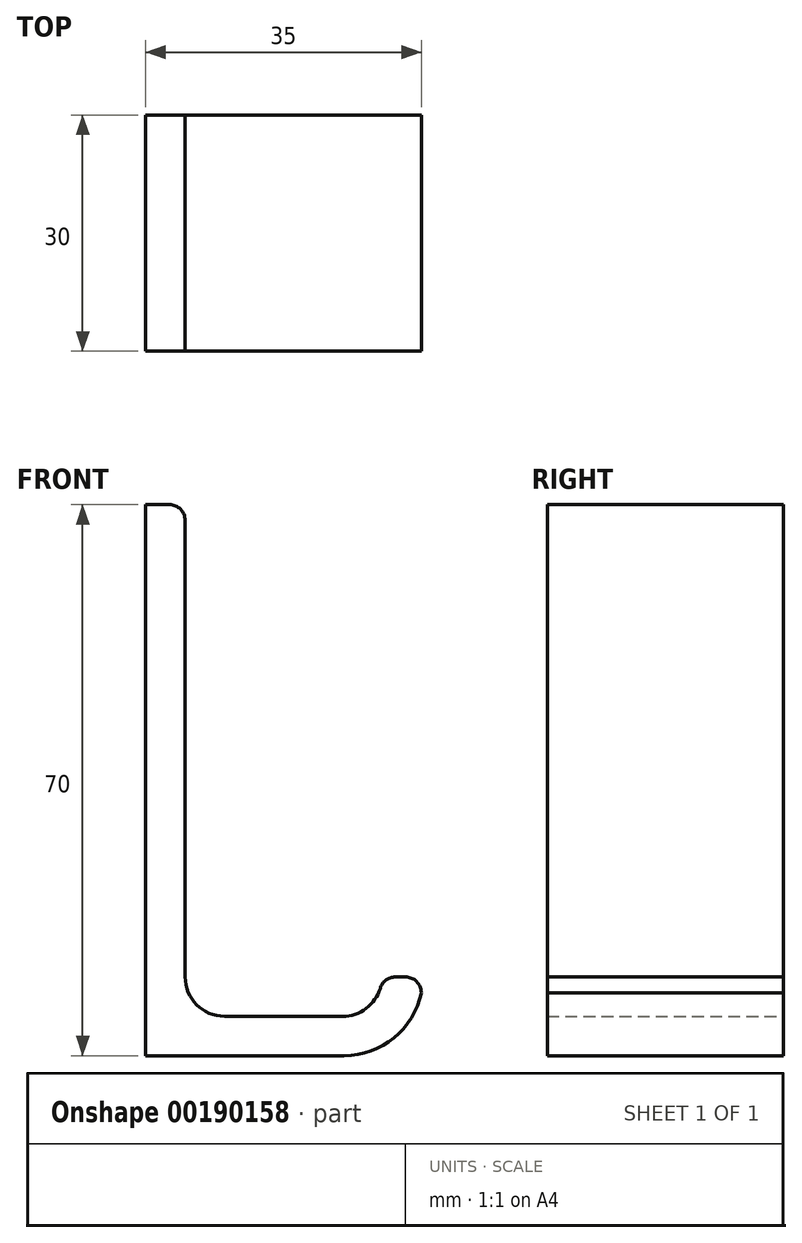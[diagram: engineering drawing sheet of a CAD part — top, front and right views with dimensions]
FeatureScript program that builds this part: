
annotation { "Feature Type Name" : "Feature", "Feature Type Description" : "" }
export const myFeature = defineFeature(function(context is Context, id is Id, definition is map)
    precondition{}
    {
        {
            var Q0;
            Q0=qCreatedBy(makeId("Front.planeOp"),FACE);
            var sketch = newSketch(context, id + "F0", { "sketchPlane" : qUnion([Q0])});
            skLineSegment(sketch, "E0.top", {"start": v(0, 70) * mm, "end": v(5, 70) * mm});
            skLineSegment(sketch, "E0.left", {"start": v(0, 0) * mm, "end": v(0, 70) * mm});
            skLineSegment(sketch, "E0.right", {"start": v(5, 5) * mm, "end": v(5, 70) * mm});
            skLineSegment(sketch, "E1.top", {"start": v(5, 5) * mm, "end": v(30, 5) * mm});
            skLineSegment(sketch, "E2.top", {"start": v(35, 10) * mm, "end": v(30, 10) * mm});
            skLineSegment(sketch, "E2.right", {"start": v(30, 5) * mm, "end": v(30, 10) * mm});
            skLineSegment(sketch, "E3", {"start": v(35, 10) * mm, "end": v(35, 0) * mm});
            skLineSegment(sketch, "E4", {"start": v(35, 0) * mm, "end": v(0, 0) * mm});
            skSolve(sketch);
        }
        {
            var Q0;
            Q0=qSketchRegion(id+"F0",true);
            extrude(context, id + "F1", {"entities" : qUnion([Q0]), "depth" : 30 * mm});
        }
        {
            var Q0;
            Q0=makeQuery(id+"F1.opExtrude","SWEPT_EDGE",EDGE,{"disambiguationData":[OSD([sQuery(id+"F0.wireOp",EDGE,"E0.right"),sQuery(id+"F0.wireOp",EDGE,"E1.top")])]});
            var Q1;
            Q1=makeQuery(id+"F1.opExtrude","SWEPT_EDGE",EDGE,{"disambiguationData":[OSD([sQuery(id+"F0.wireOp",EDGE,"E1.top"),sQuery(id+"F0.wireOp",EDGE,"E2.right")])]});
            fillet(context, id + "F2", {"entities" : qUnion([Q0, Q1]), "radius" : 5 * mm, "tangentPropagation" : true, "allowEdgeOverflow" : false});
        }
        {
            var Q0;
            Q0=makeQuery(id+"F2.opFillet","BLEND_EDGE",EDGE,{"blendedFrom":[makeQuery(id+"F1.opExtrude","SWEPT_EDGE",EDGE,{"disambiguationData":[OSD([sQuery(id+"F0.wireOp",EDGE,"E1.top"),sQuery(id+"F0.wireOp",EDGE,"E2.right")])]}),makeQuery(id+"F1.opExtrude","SWEPT_FACE",FACE,{"disambiguationData":[OSD([sQuery(id+"F0.wireOp",EDGE,"E2.top")])]})],"blendedInto":[makeQuery(id+"F1.opExtrude","SWEPT_FACE",FACE,{"disambiguationData":[OSD([sQuery(id+"F0.wireOp",EDGE,"E2.top")])]})]});
            var Q1;
            Q1=makeQuery(id+"F1.opExtrude","SWEPT_EDGE",EDGE,{"disambiguationData":[OSD([sQuery(id+"F0.wireOp",EDGE,"E2.top"),sQuery(id+"F0.wireOp",EDGE,"E3")])]});
            var Q2;
            Q2=makeQuery(id+"F1.opExtrude","SWEPT_EDGE",EDGE,{"disambiguationData":[OSD([sQuery(id+"F0.wireOp",EDGE,"E0.top"),sQuery(id+"F0.wireOp",EDGE,"E0.right")])]});
            fillet(context, id + "F3", {"entities" : qUnion([Q0, Q1, Q2]), "radius" : 2 * mm, "tangentPropagation" : true, "allowEdgeOverflow" : false});
        }
        {
            var Q0;
            Q0=makeQuery(id+"F1.opExtrude","SWEPT_EDGE",EDGE,{"disambiguationData":[OSD([sQuery(id+"F0.wireOp",EDGE,"E3"),sQuery(id+"F0.wireOp",EDGE,"E4")])]});
            fillet(context, id + "F4", {"entities" : qUnion([Q0]), "radius" : 10 * mm, "tangentPropagation" : true, "allowEdgeOverflow" : false});
        }
    });
